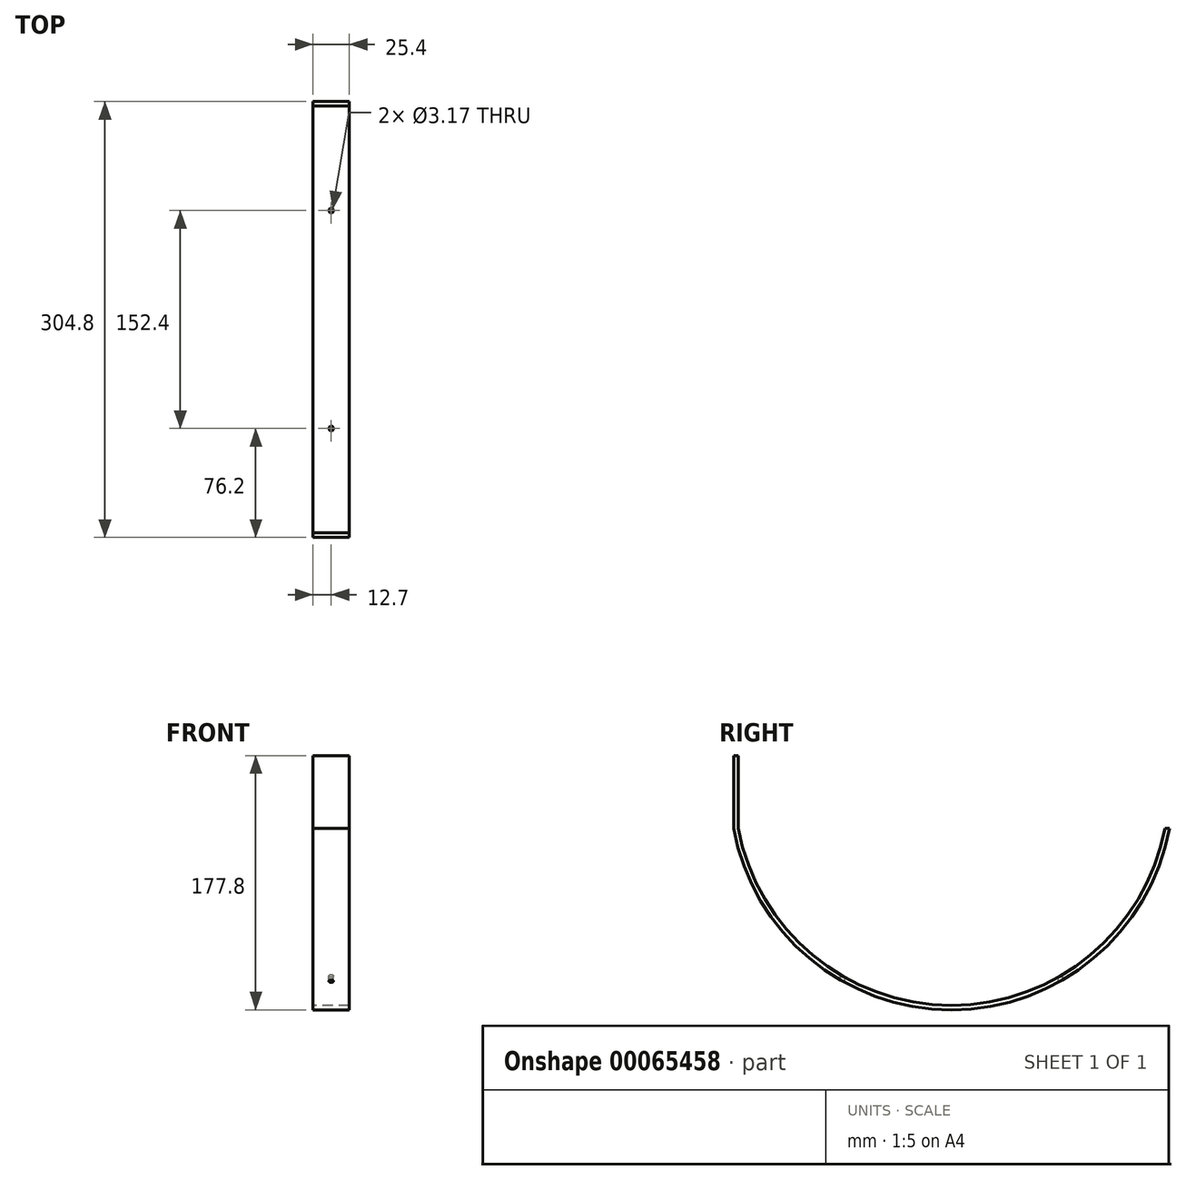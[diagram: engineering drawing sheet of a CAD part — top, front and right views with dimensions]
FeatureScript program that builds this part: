
annotation { "Feature Type Name" : "Feature", "Feature Type Description" : "" }
export const myFeature = defineFeature(function(context is Context, id is Id, definition is map)
    precondition{}
    {
        {
            var Q0;
            Q0=qCreatedBy(makeId("Right.planeOp"),FACE);
            var sketch = newSketch(context, id + "F0", { "sketchPlane" : qUnion([Q0])});
            skLineSegment(sketch, "E0", {"start": v(0, 0) * mm, "end": v(3.18, 0) * mm});
            skArc(sketch, "E1", {"start": v(0, 0) * mm, "mid": v(152.4, -127) * mm, "end": v(304.8, 0) * mm});
            skLineSegment(sketch, "E2", {"start": v(304.8, 0) * mm, "end": v(301.63, 0) * mm});
            skArc(sketch, "E3", {"start": v(3.18, 0) * mm, "mid": v(152.4, -123.82) * mm, "end": v(301.63, 0) * mm});
            skLineSegment(sketch, "E4", {"start": v(152.4, -127) * mm, "end": v(152.4, -123.82) * mm});
            skLineSegment(sketch, "E5.trimOffspring", {"start": v(301.63, 0) * mm, "end": v(304.8, 0) * mm});
            skSolve(sketch);
        }
        {
            var Q0;
            {var subQ0=sQuery(id+"F0.wireOp",EDGE,"E0");Q0=makeQuery(id+"F0.imprint","IMPRINT",FACE,{"disambiguationData":[TD([[makeQuery(id+"F0.imprint","IMPRINT",EDGE,{"derivedFrom":subQ0}),-1.0]])]});}
            var Q1;
            {var subQ2=sQuery(id+"F0.wireOp",EDGE,"E4");Q1=makeQuery(id+"F0.imprint","IMPRINT",FACE,{"disambiguationData":[TD([[makeQuery(id+"F0.imprint","IMPRINT",EDGE,{"derivedFrom":subQ2}),-1.0]])]});}
            extrude(context, id + "F1", {"entities" : qUnion([Q0, Q1]), "depth" : 25.4 * mm});
        }
        {
            var Q0;
            Q0=makeQuery(id+"F1.opExtrude","SWEPT_FACE",FACE,{"disambiguationData":[OSD([sQuery(id+"F0.wireOp",EDGE,"E0")])]});
            var Q1;
            Q1=makeQuery(id+"F1.opExtrude","SWEPT_FACE",FACE,{"disambiguationData":[OSD([sQuery(id+"F0.wireOp",EDGE,"E5.trimOffspring")])]});
            extrude(context, id + "F2", {"entities" : qUnion([Q0, Q1]), "operationType" : NewBodyOperationType.ADD, "depth" : 50.8 * mm});
        }
        {
            var Q0;
            Q0=makeQuery(id+"F2.opExtrude","SWEPT_FACE",FACE,{"disambiguationData":[OSD([sQuery(id+"F0.wireOp",EDGE,"E1"),sQuery(id+"F0.wireOp",EDGE,"E5.trimOffspring")])]});
            var sketch = newSketch(context, id + "F3", { "sketchPlane" : qUnion([Q0])});
            skLineSegment(sketch, "E6", {"start": v(-12.7, 50.8) * mm, "end": v(-12.7, 38.1) * mm});
            skLineSegment(sketch, "E7", {"start": v(-12.7, 38.1) * mm, "end": v(-12.7, 12.7) * mm});
            skSolve(sketch);
        }
        {
            var Q0;
            Q0=sQuery(id+"F3.wireOp",VERTEX,"E7.start");
            var Q1;
            Q1=sQuery(id+"F3.wireOp",VERTEX,"E7.end");
            var Q2;
            Q2=makeQuery(id+"F1.opExtrude","SWEPT_BODY",BODY,{"disambiguationData":[OSD([sQuery(id+"F0.wireOp",EDGE,"E1"),sQuery(id+"F0.wireOp",EDGE,"E0"),sQuery(id+"F0.wireOp",EDGE,"E3"),sQuery(id+"F0.wireOp",EDGE,"E5.trimOffspring")])]});
            hole(context, id + "F4", {"style" : HoleStyle.SIMPLE, "holeDiameter" : 3.17 * mm, "endStyle" : HoleEndStyle.THROUGH, "locations" : qUnion([Q0, Q1]), "scope" : qUnion([Q2])});
        }
        {
            var Q0;
            Q0=qCreatedBy(makeId("Top.planeOp"),FACE);
            var sketch = newSketch(context, id + "F5", { "sketchPlane" : qUnion([Q0])});
            skLineSegment(sketch, "E8", {"start": v(0, 0) * mm, "end": v(0, 304.8) * mm});
            skLineSegment(sketch, "E9", {"start": v(0, 0) * mm, "end": v(0, 76.2) * mm});
            skLineSegment(sketch, "E10", {"start": v(0, 76.2) * mm, "end": v(0, 228.6) * mm});
            skLineSegment(sketch, "E11", {"start": v(0, 76.2) * mm, "end": v(12.7, 76.2) * mm});
            skLineSegment(sketch, "E12", {"start": v(12.7, 76.2) * mm, "end": v(12.7, 228.6) * mm});
            skSolve(sketch);
        }
        {
            var Q0;
            Q0=sQuery(id+"F5.wireOp",VERTEX,"E12.start");
            var Q1;
            Q1=sQuery(id+"F5.wireOp",VERTEX,"E12.end");
            var Q2;
            Q2=makeQuery(id+"F1.opExtrude","SWEPT_BODY",BODY,{"disambiguationData":[OSD([sQuery(id+"F0.wireOp",EDGE,"E1"),sQuery(id+"F0.wireOp",EDGE,"E0"),sQuery(id+"F0.wireOp",EDGE,"E3"),sQuery(id+"F0.wireOp",EDGE,"E5.trimOffspring")])]});
            hole(context, id + "F6", {"style" : HoleStyle.SIMPLE, "holeDiameter" : 3.17 * mm, "endStyle" : HoleEndStyle.THROUGH, "locations" : qUnion([Q0, Q1]), "scope" : qUnion([Q2])});
        }
    });
